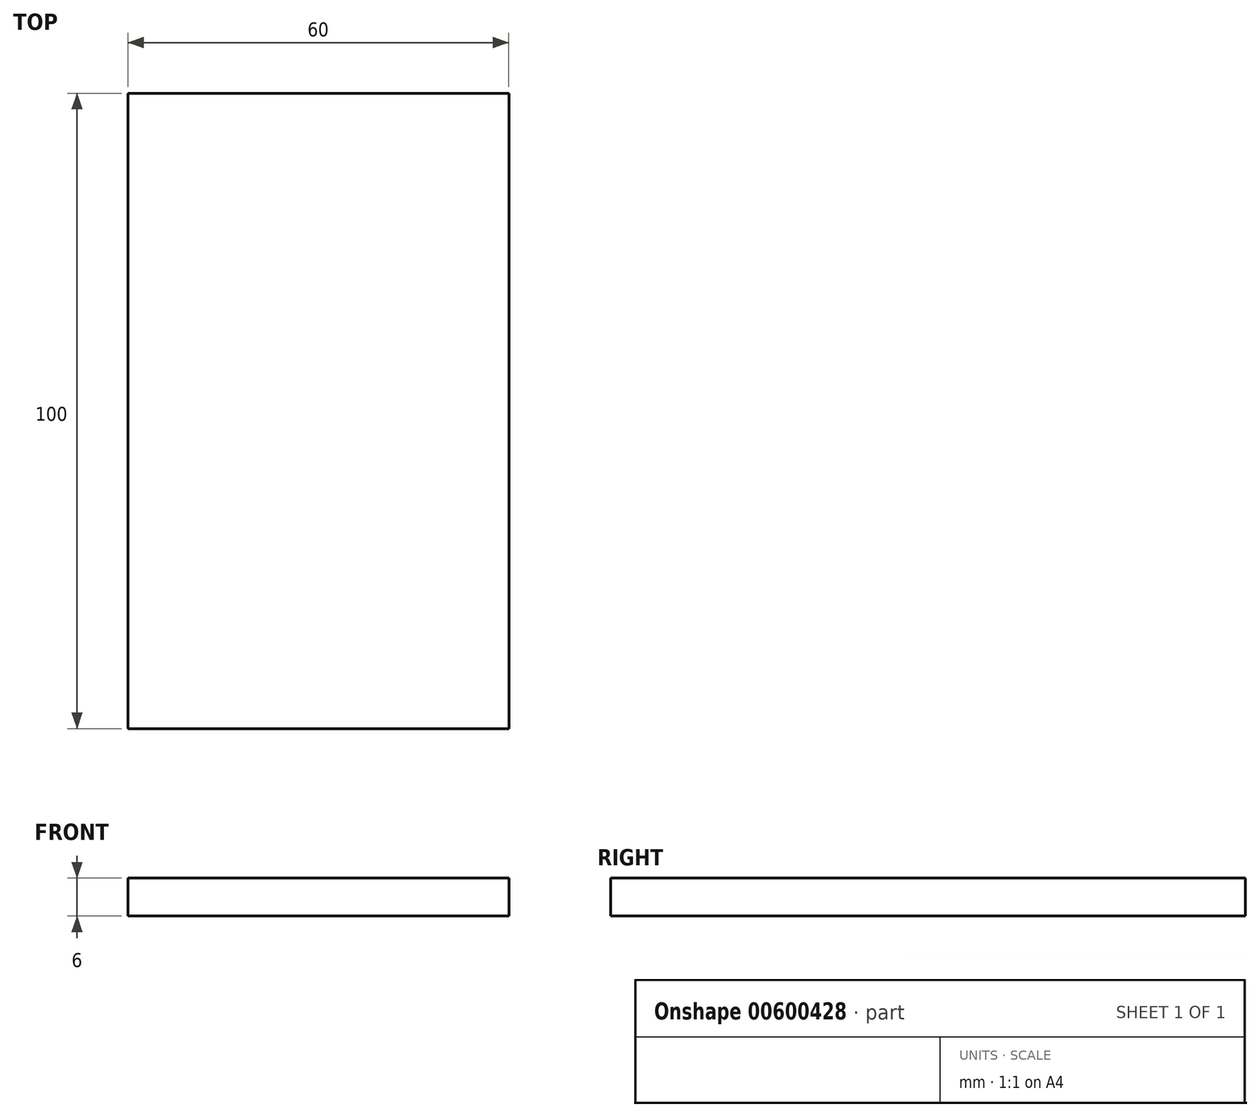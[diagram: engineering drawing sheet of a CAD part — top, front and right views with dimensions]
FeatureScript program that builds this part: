
annotation { "Feature Type Name" : "Feature", "Feature Type Description" : "" }
export const myFeature = defineFeature(function(context is Context, id is Id, definition is map)
    precondition{}
    {
        {
            var Q0;
            Q0=qCreatedBy(makeId("Top.planeOp"),FACE);
            var sketch = newSketch(context, id + "F0", { "sketchPlane" : qUnion([Q0])});
            skLineSegment(sketch, "E0.bottom", {"start": v(-121.32, 56.37) * mm, "end": v(-61.32, 56.37) * mm});
            skLineSegment(sketch, "E0.top", {"start": v(-121.32, -43.63) * mm, "end": v(-61.32, -43.63) * mm});
            skLineSegment(sketch, "E0.left", {"start": v(-121.32, 56.37) * mm, "end": v(-121.32, -43.63) * mm});
            skLineSegment(sketch, "E0.right", {"start": v(-61.32, 56.37) * mm, "end": v(-61.32, -43.63) * mm});
            skSolve(sketch);
        }
        {
            var Q0;
            Q0 = qSketchRegion(id + "F0", true);
            extrude(context, id + "F1", {"entities" : qUnion([Q0]), "depth" : 6 * mm, "offsetDistance" : 25 * mm});
        }
    });
